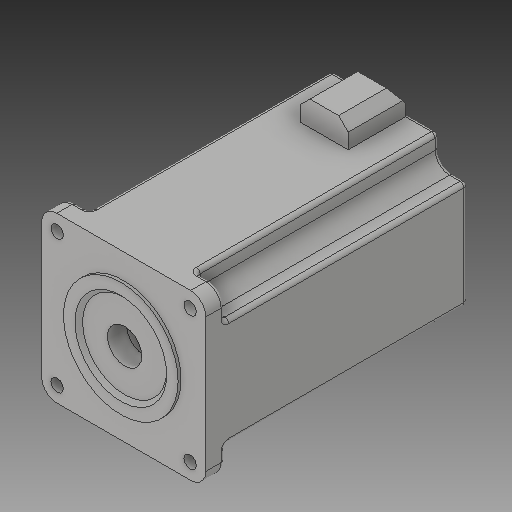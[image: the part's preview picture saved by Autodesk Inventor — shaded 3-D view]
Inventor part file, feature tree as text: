
AUTODESK INVENTOR PART (.ipt)
format: ipt  version: 2018 (Build 220112000, 112)  size: 387,584 bytes
history: native  units: mm
features: extrude x13, sketch x13, chamfer x5, projected_geometry x4, fillet x3, hole x1, plane x1
ambient origin geometry x8: Origin, YZ Plane, XZ Plane, XY Plane, X Axis, Y Axis, Z Axis, Center Point
bodies: Solid1 (feature_tree)
feature tree (40):
  extrude  "Extrusion1"  Depth=86.0mm
  extrude  "Extrusion2"  Depth=140.0mm
  extrude  "Extrusion3"  Depth=1.5mm
  hole  "Hole1"  [1 undecoded]
  plane  "Work Plane1"
  extrude  "Extrusion4"  Depth=13.0mm TaperAngle=0.0deg
  sketch  "Sketch6"  dims[d13=3.0mm d14=6.0mm d15=4.0mm d16=2.0mm d17=90.0deg d18=13.0mm d19=0.0mm d24=2.438mm d25=0.0mm]
  extrude  "Extrusion6"  Depth=69.6mm
  extrude  "Extrusion7"  Depth=120.0mm TaperAngle=0.0deg
  chamfer  "Chamfer1"  Distance=13.0mm
  fillet  "Fillet1"  Radius=8.0mm
  chamfer  "Chamfer2"  Distance=5.0mm Angle=45.0deg
  chamfer  "Chamfer3"  Distance=1.0mm Angle=45.0deg
  extrude  "Extrusion8"  Depth=56.0mm
  extrude  "Extrusion9"  Depth=3.0mm TaperAngle=45.0deg
  chamfer  "Chamfer4"  Distance=2.0mm
  fillet  "Fillet3"  Radius=15.0mm
  extrude  "Extrusion10"  Depth=15.0mm
  fillet  "Fillet4"  Radius=40.0mm
  extrude  "Extrusion11"  Depth=130.0mm TaperAngle=0.0deg
  chamfer  "Chamfer5"  Distance=2.0mm
  extrude  "Extrusion13"  Depth=8.0mm
  extrude  "Extrusion14"  Depth=2.0mm TaperAngle=0.0deg
  extrude  "Extrusion15"  Depth=2.0mm TaperAngle=45.0deg
  sketch  "Sketch1"  dims[d0=86.0mm d1=86.0mm]
  sketch  "Sketch2"  dims[d2=140.0mm d3=0.0mm d5=60.0mm]
  sketch  "Sketch3"  dims[d6=1.5mm d7=0.0mm d8=14.0mm]
  sketch  "Sketch5"  dims[d9=40.0mm d10=0.0mm d11=10.0mm d12=10.0mm]
  projected_geometry  "Projected Loop1"
  sketch  "Sketch7"  dims[d36=6.5mm d37=69.6mm]
  projected_geometry  "Projected Loop2"
  sketch  "Sketch8"  dims[d38=69.6mm d39=120.0mm d40=0.0mm]
  sketch  "Sketch9"  dims[d41=25.0mm]
  projected_geometry  "Projected Loop3"
  sketch  "Sketch10"  dims[d42=30.0mm]
  sketch  "Sketch11"  dims[d43=5.0mm d46=13.0mm d47=0.0mm]
  sketch  "Sketch13"  dims[d48=5.0mm d49=7.0mm d50=45.0deg d51=8.0mm d53=5.0mm d54=7.0mm d55=45.0deg d56=1.0mm d57=7.0mm d58=45.0deg]
  projected_geometry  "Projected Loop5"
  sketch  "Sketch14"  dims[d59=3.0mm d60=0.0mm d61=56.0mm]
  sketch  "Sketch15"  dims[d62=3.0mm d63=0.0mm d64=3.0mm d65=7.0mm d66=45.0deg d67=2.0mm d71=15.0mm d72=15.0mm d73=40.0mm d75=360.0deg d77=130.0mm d78=0.0mm d79=2.0mm d81=8.0mm d82=2.0mm d83=0.0mm d84=2.0mm d85=7.0mm d86=45.0deg d90=13.0mm d91=10.0mm d92=0.0mm d93=10.0mm d94=0.0mm d95=10.0mm d96=0.0mm]
note: 1 required parameter value undecoded (feature->parameter linkage not recoverable at this tier; creation-order binding heuristic only, values carry confidence <= 0.55)
